# Revit family: Faucet-Lavatory-KOHLER-Finial_Traditional-K-310_1
name_source: partatom
category: Plumbing Fixtures
revit_build: Autodesk Revit 2015 (Build: 20140606_1530(x64)
units: mm (PartAtom-declared; Revit-internal decimal feet)

## types (6) — shared parameters
ADA Compliant = Yes
Assembly Code = D2010
CW Connection = Yes
Cold Water Inlet = Cold Water Inlet
Date Modified = 12/27/2018
Default Elevation = 36"
Description = Widespread bathroom sink faucet with lever handles
Drain Included = Yes
Flow Rate = 1 GPM
HW Connection = Yes
Handle Clearance = 3 1/4"
Height = 6 1/4"
Hot Water Inlet = Hot Water Inlet
Length = 5"
Manufacturer = KOHLER Co.
MasterFormat 1995 = 15410
MasterFormat 2004 = 22.41.39
Material = Premium Metal Construction
Pressure = 60.00 psi
Product Documentation Link = http://www.us.kohler.com
Product Name = Finial Traditional
Product Page URL = http://www.us.kohler.com
Spout Reach = 5"
URL = https://www.us.kohler.com
Vent Connection = No
Waste Connection = No
Waste Water Outlet = Waste Water Outlet

## per-type parameters (varying)
| type | Finish | Model | Type |
| CP-Polished Chrome | Kohler-Metal-CP-Polished_Chrome | K-310-4M-CP | 1 |
| SN-Vibrant Polished Nickel | Kohler-Metal-SN-Vibrant_Polished_Nickel | K-310-4M-SN | 2 |
| AF-Vibrant French Gold | Kohler-Metal-AF-Vibrant_French_Gold | K-310-4M-AF | 3 |
| BN-Vibrant Brushed Nickel | Kohler-Metal-BN-Vibrant_Brushed_Nickel | K-310-4M-BN | 4 |
| BV-Vibrant Brushed Bronze | Kohler-Metal-BV-Brushed_Bronze | K-310-4M-BV | 5 |
| 2BZ-Oil-Rubbed Bronze | Kohler-Metal-2BZ-Oil_Rubbed_Bronze | K-310-4M-2BZ | 6 |

## geometry (parser evidence)
native form markers: Sweep x7
no freeform markers — native parametric forms only
